# Revit family: KS Husky, Typ VI-32, M10-M12, Ø114,3-Ø168,3
name_source: partatom
category: HLS-Bauteile
revit_build: Autodesk Revit 2017 (Build: 20190507_1515(x64)
units: mm (PartAtom-declared; Revit-internal decimal feet)

## family parameters
Arbeitsebenenbasiert = Ja
Beim Laden mit Abzugskörper schneiden = Nein
Bemaßung runder Anschluss = Durchmesser verwenden
Gemeinsam genutzt = Ja
Immer vertikal = Nein
Raumberechnungspunkt = Nein
Teiletyp = Normal

## types (3) — shared parameters
Anschluss = M10/M12
Baustoffklasse = B2
DVS = 18 mm  [stored 0.0590551 ft]
Dichte Kern = 120 kg/m³
Dämmkörper = KA/PU
Fabrikat = MEFA
HGA = 22 mm  [stored 0.0721785 ft]
Kurztext1 = Kälteschelle Husky VI 32
L = 51 mm  [stored 0.167323 ft]
MB = 35 mm  [stored 0.114829 ft]
MD = 4 mm  [stored 0.0131234 ft]
Material = Stahl
Material Mantel = Kunststoff
Materialname = S235
Mengeneinheit = St
Oberflaeche = galvanisch verzinkt
Rohrschellentyp = Maxima PSM
Schalenlänge = 51 mm
Typ = VI 32
Vorgabe-Ansicht = 1219 mm
Wasserdampfdiffusionswiderstand = 7000 µ
Wärmeleitfähigkeit = 0.029 W/mK
max. Temperaturbeständigkeit = 105 °C
stat. Belastung Kern = 0,27 N/mm²
zero-valued in all types: Nennweite DN Rohr, Rohraußendurchmesser, Stärke Material

## per-type parameters (varying)
| type | A | AB | Artikelnummer | B | Breite | D | D0 | DF1 | DF2 | DS | Dmax | Dmin | EAN | Gewicht | Gewicht pro Bauteil | H | Kurztext2 | R | RM | Rohraußendurchmesser Stahl | S | max. zul. Last | vpe |
| KS Husky,Typ VI-32,M10-M12,Ø114,3 | 67 mm | 1 mm  [stored 0.00328084 ft] | 6851140 | 273 mm | 272 mm | 114 mm | 197 mm | 33 mm | 33 mm | 41 mm | 116 mm | 113 mm | 4250928441065 | 1.09 kg | 1.09 kg | 227 mm | 114,3 mm Iso 41 x 51 mm M10/M12 | 99 mm | 103 mm | 114,3 mm | 240 mm | 1.45 kN | 4 St |
| KS Husky,Typ VI-32, M10-M12,Ø139,7 | 68 mm | 2 mm  [stored 0.00656168 ft] | 6851400 | 298 mm | 297 mm | 140 mm | 224 mm | 32 mm  [stored 0.104987 ft] | 32 mm  [stored 0.104987 ft] | 42 mm | 142 mm | 138 mm | 4250928441072 | 1.20 kg | 1.20 kg | 254 mm | 139,7 mm Iso 42 x 51 mm M10/M12 | 112 mm | 116 mm | 139,7 mm | 266 mm | 1.78 kN | 4 St |
| KS Husky,Typ VI-32, M10-M12,Ø168,3 | 71 mm | 1 mm  [stored 0.00328084 ft] | 6851680 | 330 mm | 331 mm | 168 mm | 258 mm | 31 mm | 31 mm | 45 mm | 170 mm | 167 mm | 4250928441089 | 1.36 kg | 1.36 kg | 288 mm | 168,3 mm Iso 45 x 51 mm M10/M12 | 129 mm | 133 mm | 168,3 mm | 299 mm | 2.14 kN | 2 St |

note: [stored X ft] marks values corroborated as IEEE doubles in the binary element streams (Revit-internal decimal feet)

## geometry (parser evidence)
native form markers: Sweep x4
no freeform markers — native parametric forms only
